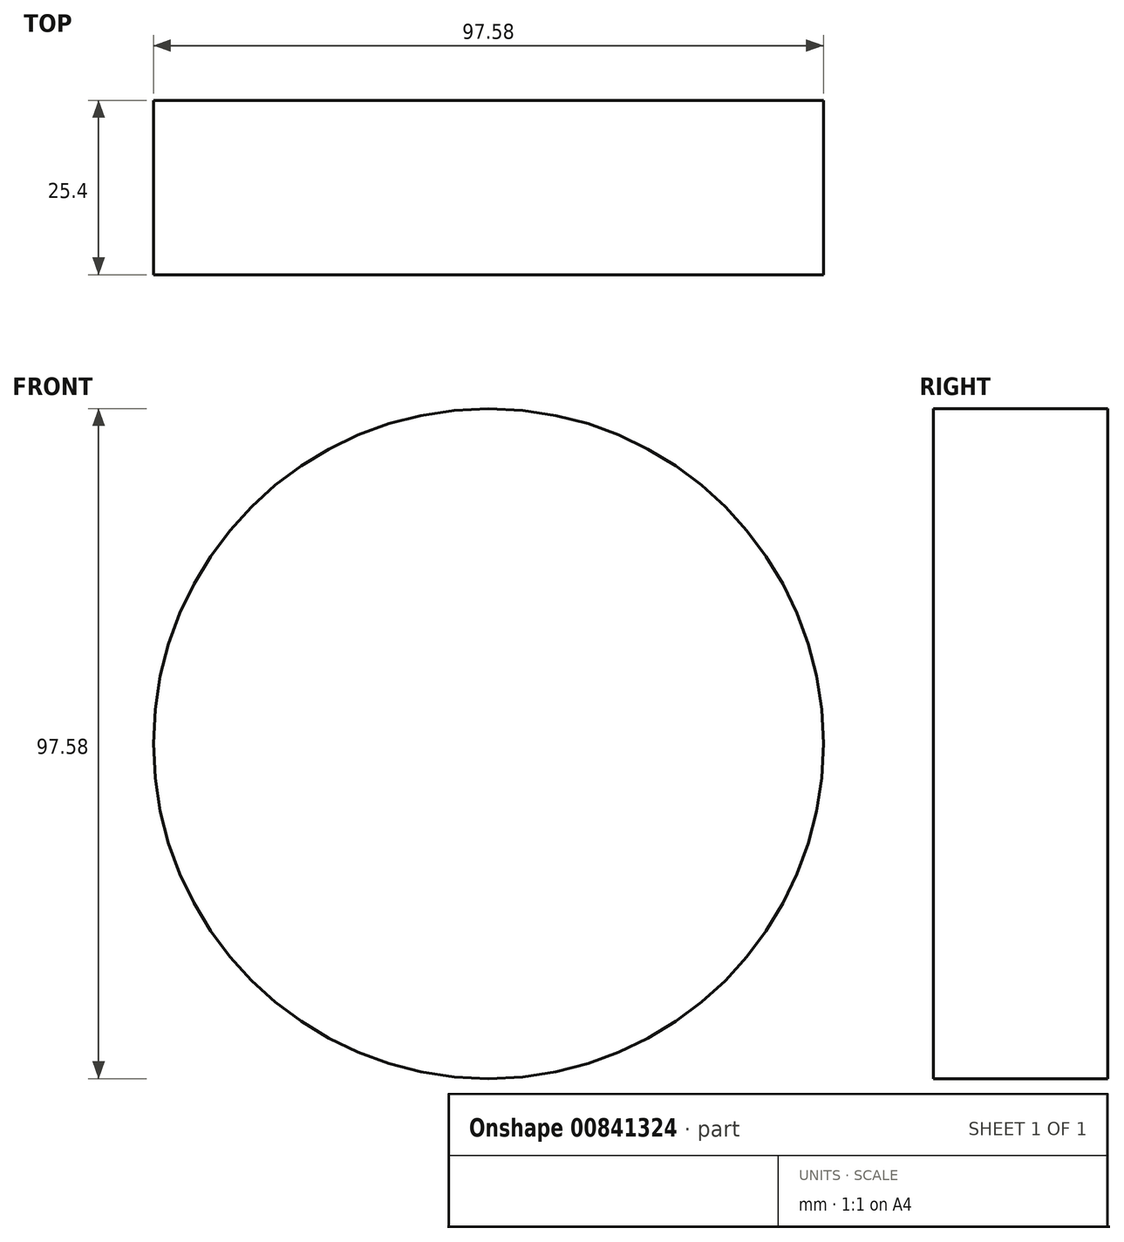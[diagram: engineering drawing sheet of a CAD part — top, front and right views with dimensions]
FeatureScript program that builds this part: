
annotation { "Feature Type Name" : "Feature", "Feature Type Description" : "" }
export const myFeature = defineFeature(function(context is Context, id is Id, definition is map)
    precondition{}
    {
        {
            var Q0;
            Q0=qCreatedBy(makeId("Front.planeOp"),FACE);
            var sketch = newSketch(context, id + "F0", { "sketchPlane" : qUnion([Q0])});
            skCircle(sketch, "E0", {"center": v(-3.8, 0) * mm, "radius": 48.79 * mm});
            skSolve(sketch);
        }
        {
            var Q0;
            Q0=makeQuery(id+"F0.imprint","IMPRINT",FACE,{"disambiguationData":[TD([[makeQuery(id+"F0.imprint","IMPRINT",EDGE,{"derivedFrom":sQuery(id+"F0.wireOp",EDGE,"E0")}),1.0]])]});
            extrude(context, id + "F1", {"entities" : qUnion([Q0]), "depth" : 25.4 * mm, "offsetDistance" : 25.4 * mm});
        }
        {
            var Q0;
            Q0=makeQuery(id+"F1.opExtrude","CAP_FACE",FACE,{"disambiguationData":[OSD([sQuery(id+"F0.wireOp",EDGE,"E0")])],"isStart":false});
            var sketch = newSketch(context, id + "F2", { "sketchPlane" : qUnion([Q0])});
            skSolve(sketch);
        }
        {
            var Q0;
            Q0=makeQuery(id+"F2.imprint","IMPRINT",FACE,{"disambiguationData":[TD([[makeQuery(id+"F2.imprint","IMPRINT",EDGE,{"derivedFrom":makeQuery(id+"F1.opExtrude","CAP_EDGE",EDGE,{"disambiguationData":[OSD([sQuery(id+"F0.wireOp",EDGE,"E0")])],"isStart":false})}),1.0]])]});
            var sketch = newSketch(context, id + "F3", { "sketchPlane" : qUnion([Q0])});
            skCircle(sketch, "E1", {"center": v(-10.9, 0) * mm, "radius": 27.11 * mm});
            skSolve(sketch);
        }
        {
            var Q0;
            Q0=sQuery(id+"F3.wireOp",EDGE,"E1");
            extrude(context, id + "F4", {"bodyType" : ToolBodyType.SURFACE, "surfaceEntities" : qUnion([Q0]), "depth" : 127 * mm, "offsetDistance" : 25.4 * mm});
        }
    });
